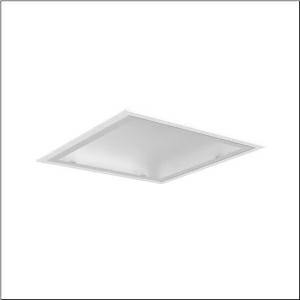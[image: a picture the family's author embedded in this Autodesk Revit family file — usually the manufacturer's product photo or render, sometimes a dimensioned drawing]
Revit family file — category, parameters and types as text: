
# Revit family: mira_11_51fr127a471a
name_source: partatom
category: Lighting Fixtures
units: mm (PartAtom-declared; Revit-internal decimal feet)

## family parameters
Cut with Voids When Loaded = No
Host = Face
Light Source = No
Part Type = Normal
Room Calculation Point = No
Round Connector Dimension = Use Diameter
Shared = No

## types (1)
- Mira 11 (1 x LED, 7290 lm, 66 W, 4000K)
    Apparent Load = 66 VA
    CIE Flux Codes = 51 82 97 100 100
    Color Rendering = 80
    Color Temperature = 4000K
    Default Elevation = 1800 mm
    Description = Mira 11, clean room luminaire, primary light control with reflector, primary optical cover: cover, of toughened safety glass, light emission: direct distribution, primary light characteristic: symmetric, installation type: recessed, LED, rated luminous flux: 7.290lm, luminous efficacy: 111lm/W, light colour: 840, colour temperature: 4000K, control gear: ON/OFF, with terminal, 3-pole, max. 2.5mm², mains connection: 230V, AC, 50/60Hz, rated input power: 66W, luminaire housing, of sheet steel, coated, pure white (RAL 9010), with concealed magnets, module: M625, length: 623mm, width: 623mm, height: 90mm, protection rating (complete): IP65, insulation class (complete): insulation class I (protective earthing), certification: CE, UKCA, permissible operating ambient temperature: -5..+40°C, standard: EN 50419, packaging unit: 1 piece
    Height = 0 mm  [stored 0 ft]
    Lamp = 1 x LED
    Lamp Light Flux = 7290 lm
    Lamp Power = 66 W
    Lamp count = 1
    Length = 625 mm
    Luminous efficacy = 110 lm/W
    Manufacturer = Siteco
    ModVariant = No
    Model = 51FR127A471A
    Mounting Place = Ceiling
    Mounting Type = Recessed
    Number of Poles = 1
    OnlyDefault = Yes
    Power Factor = 1
    Product Name = Mira 11
    Product group = clean room luminaire | ceiling recessed
    ProductGroupID = 402
    Protection Class = Protection class I
    Protection Degree = IP 65
    RLX_Detail_Level = 1
    RLX_Emergency_Light_Flux = 0 lm
    RLX_Emergency_Type = 0
    RLX_Emergency_Type_DB = No
    RlxData = <blob elided: 19289 chars, md5=f0b93453>
    Socket = socket
    Standby Power = 0 W
    System Light Flux = 7290 lm
    System Power = 66 W
    Type Comments = Product without accessories
    Type Image = l_1006636.jpg
    URL = http://relux.com
    VarID = ---
    Voltage = 0 V
    Weight = 0.00 kg
    Width = 625 mm

note: [stored X ft] marks values corroborated as IEEE doubles in the binary element streams (Revit-internal decimal feet)

## geometry (parser evidence)
native form markers: Blend x4, Sweep x9
no freeform markers — native parametric forms only
